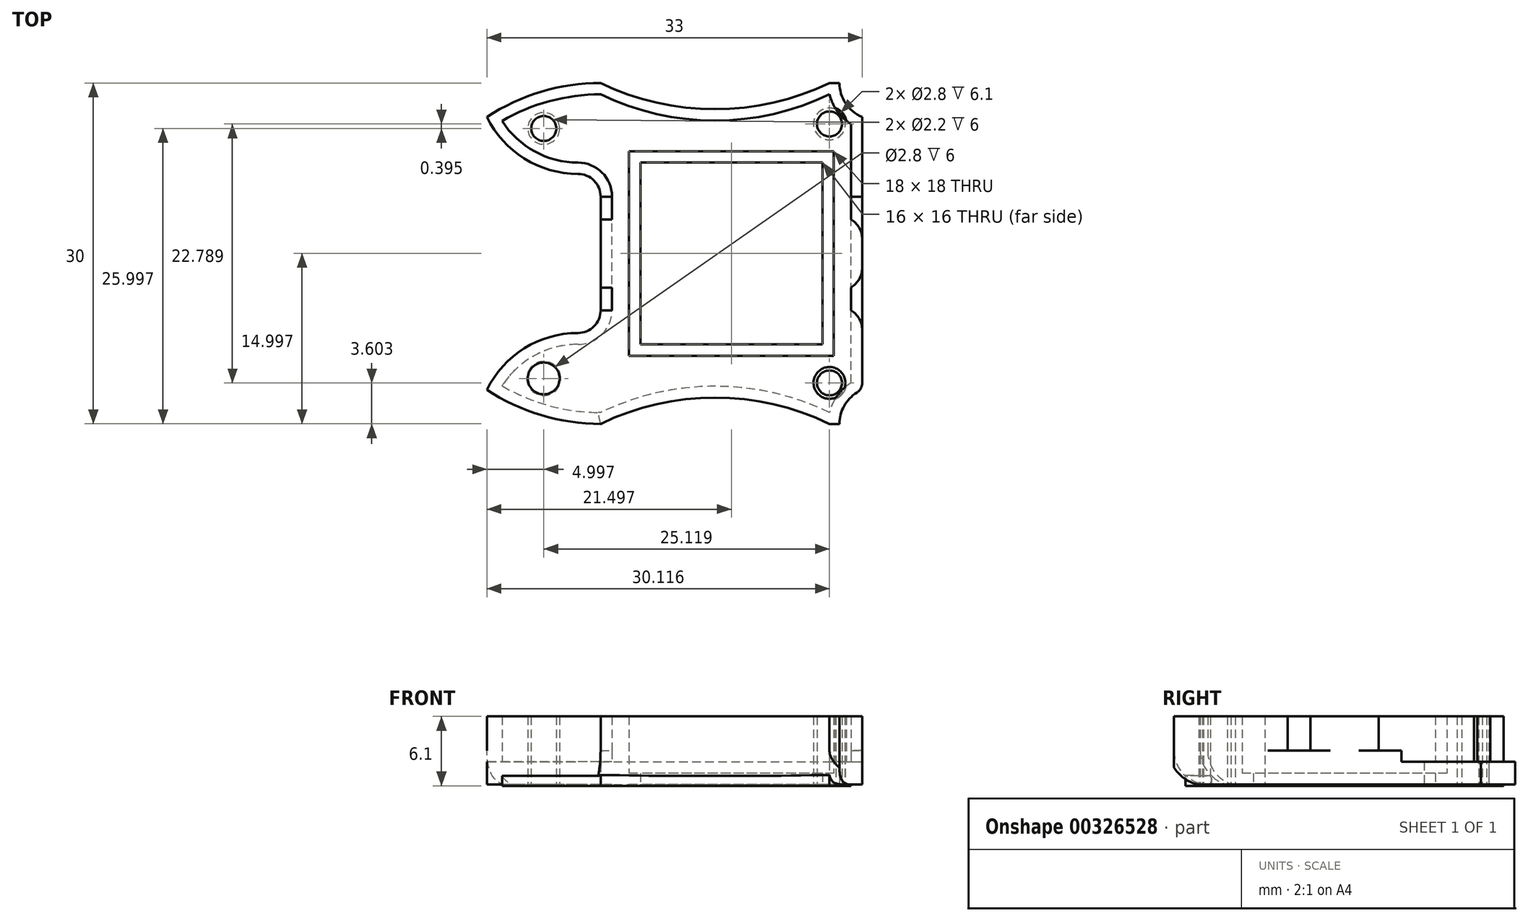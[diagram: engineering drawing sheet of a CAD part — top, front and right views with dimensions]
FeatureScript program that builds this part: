
annotation { "Feature Type Name" : "Feature", "Feature Type Description" : "" }
export const myFeature = defineFeature(function(context is Context, id is Id, definition is map)
    precondition{}
    {
        {
            var Q0;
            Q0=qCreatedBy(makeId("Top.planeOp"),FACE);
            var sketch = newSketch(context, id + "F0", { "sketchPlane" : qUnion([Q0])});
            skArc(sketch, "E0.MirrorCS", {"start": v(-70, 2.38) * mm, "mid": v(-65.22, 4.61) * mm, "end": v(-60, 5.38) * mm});
            skArc(sketch, "E1.MirrorCS", {"start": v(-62, -2.62) * mm, "mid": v(-66.72, -1.27) * mm, "end": v(-70, 2.38) * mm});
            skArc(sketch, "E2.MirrorCS", {"start": v(-62, -16.62) * mm, "mid": v(-66.72, -17.98) * mm, "end": v(-70, -21.62) * mm});
            skArc(sketch, "E3.MirrorCS", {"start": v(-70, -21.62) * mm, "mid": v(-65.22, -23.86) * mm, "end": v(-60, -24.62) * mm});
            skArc(sketch, "E4.MirrorCS", {"start": v(-62, -16.62) * mm, "mid": v(-60.59, -16.04) * mm, "end": v(-60, -14.62) * mm});
            skArc(sketch, "E5.MirrorCS", {"start": v(-62, -2.62) * mm, "mid": v(-60.59, -3.2) * mm, "end": v(-60, -4.62) * mm});
            skArc(sketch, "E6.MirrorCS", {"start": v(-37, -21.62) * mm, "mid": v(-38.46, -22.82) * mm, "end": v(-39, -24.62) * mm});
            skArc(sketch, "E7.MirrorCS", {"start": v(-37, 2.38) * mm, "mid": v(-38.46, 3.57) * mm, "end": v(-39, 5.38) * mm});
            skLineSegment(sketch, "E8", {"start": v(-37, 2.38) * mm, "end": v(-37, -4.62) * mm});
            skLineSegment(sketch, "E9", {"start": v(-37, -21.62) * mm, "end": v(-37, -14.62) * mm});
            skLineSegment(sketch, "E10", {"start": v(-39.88, -24.62) * mm, "end": v(-39, -24.62) * mm});
            skLineSegment(sketch, "E11", {"start": v(-39, 5.38) * mm, "end": v(-39.88, 5.38) * mm});
            skLineSegment(sketch, "E12", {"start": v(-37, -14.62) * mm, "end": v(-37, -4.62) * mm});
            skLineSegment(sketch, "E13", {"start": v(-60, -14.62) * mm, "end": v(-60, -4.62) * mm});
            skLineSegment(sketch, "E14.trimOffspring", {"start": v(-60, -4.62) * mm, "end": v(-59, -4.62) * mm});
            skLineSegment(sketch, "E15.trimOffspring", {"start": v(-60, -14.62) * mm, "end": v(-59, -14.62) * mm});
            skArc(sketch, "E16.0", {"start": v(-62, -1.62) * mm, "mid": v(-65.8, -0.65) * mm, "end": v(-68.67, 2.03) * mm});
            skArc(sketch, "E16.1", {"start": v(-62, -1.62) * mm, "mid": v(-59.88, -2.5) * mm, "end": v(-59, -4.62) * mm});
            skLineSegment(sketch, "E16.2", {"start": v(-59, -14.62) * mm, "end": v(-59, -4.62) * mm});
            skLineSegment(sketch, "E16.3", {"start": v(-38, -14.62) * mm, "end": v(-38, -4.62) * mm});
            skLineSegment(sketch, "E16.4", {"start": v(-38, 1.77) * mm, "end": v(-38, -4.62) * mm});
            skArc(sketch, "E16.5", {"start": v(-38, 1.77) * mm, "mid": v(-39.2, 2.89) * mm, "end": v(-39.88, 4.38) * mm});
            skLineSegment(sketch, "E16.7", {"start": v(-38, -21.02) * mm, "end": v(-38, -14.62) * mm});
            skArc(sketch, "E16.8", {"start": v(-38, -21.02) * mm, "mid": v(-39.2, -22.14) * mm, "end": v(-39.88, -23.62) * mm});
            skArc(sketch, "E16.10", {"start": v(-68.67, 2.03) * mm, "mid": v(-64.49, 3.78) * mm, "end": v(-60, 4.38) * mm});
            skArc(sketch, "E16.11", {"start": v(-68.67, -21.28) * mm, "mid": v(-64.49, -23.03) * mm, "end": v(-60, -23.62) * mm});
            skArc(sketch, "E16.12", {"start": v(-62, -17.62) * mm, "mid": v(-65.8, -18.6) * mm, "end": v(-68.67, -21.28) * mm});
            skArc(sketch, "E16.13", {"start": v(-62, -17.62) * mm, "mid": v(-59.88, -16.74) * mm, "end": v(-59, -14.62) * mm});
            skPoint(sketch, "E17", {"position": v(-65, 1.38) * mm});
            skPoint(sketch, "E18", {"position": v(-39.88, 1.77) * mm});
            skPoint(sketch, "E19.orphan", {"position": v(-70, 5.38) * mm});
            skLineSegment(sketch, "E20.trimOffspring", {"start": v(-60, -2.39) * mm, "end": v(-60, -2.62) * mm, "construction": true});
            skPoint(sketch, "E21.orphan", {"position": v(-60, 1.38) * mm});
            skPoint(sketch, "E22.start.orphan", {"position": v(-65, 5.38) * mm});
            skPoint(sketch, "E23.right.start.orphan", {"position": v(-70, 1.38) * mm});
            skPoint(sketch, "E23.top.end.orphan", {"position": v(-70, -2.62) * mm});
            skPoint(sketch, "E24.trimOffspring.end.orphan", {"position": v(-65, -2.62) * mm});
            skCircle(sketch, "E25", {"center": v(-65, 1.38) * mm, "radius": 1.5 * mm});
            skCircle(sketch, "E26", {"center": v(-39.88, 1.77) * mm, "radius": 1.5 * mm});
            skCircle(sketch, "E27.MirrorC", {"center": v(-65, -20.62) * mm, "radius": 1.5 * mm});
            skCircle(sketch, "E28.MirrorC", {"center": v(-39.88, -21.02) * mm, "radius": 1.5 * mm});
            skCircle(sketch, "E29.0", {"center": v(-65, -20.62) * mm, "radius": 1.4 * mm});
            skCircle(sketch, "E30.0", {"center": v(-39.88, -21.02) * mm, "radius": 1.4 * mm});
            skCircle(sketch, "E31.0", {"center": v(-39.88, 1.77) * mm, "radius": 1.4 * mm});
            skCircle(sketch, "E32.0", {"center": v(-65, 1.38) * mm, "radius": 1.4 * mm});
            skLineSegment(sketch, "E33", {"start": v(-60, -12.62) * mm, "end": v(-59, -12.62) * mm});
            skLineSegment(sketch, "E34", {"start": v(-60, -6.62) * mm, "end": v(-59, -6.62) * mm});
            skLineSegment(sketch, "E35.trimOffspring", {"start": v(-38, -12.62) * mm, "end": v(-37, -12.62) * mm});
            skLineSegment(sketch, "E36.trimOffspring", {"start": v(-38, -14.62) * mm, "end": v(-37, -14.62) * mm});
            skLineSegment(sketch, "E37.trimOffspring", {"start": v(-38, -6.62) * mm, "end": v(-37, -6.62) * mm});
            skPoint(sketch, "E38", {"position": v(-49.5, -22.31) * mm});
            skPoint(sketch, "E39", {"position": v(-49.5, -21.31) * mm});
            skArc(sketch, "E40", {"start": v(-39.88, -23.62) * mm, "mid": v(-49.94, -21.31) * mm, "end": v(-60, -23.62) * mm});
            skPoint(sketch, "E41", {"position": v(-39.88, -24.62) * mm});
            skArc(sketch, "E42", {"start": v(-39.88, -24.62) * mm, "mid": v(-49.94, -22.31) * mm, "end": v(-60, -24.62) * mm});
            skArc(sketch, "E43.MirrorCS", {"start": v(-39.88, 5.38) * mm, "mid": v(-49.94, 3.06) * mm, "end": v(-60, 5.38) * mm});
            skArc(sketch, "E44.MirrorCS", {"start": v(-39.88, 4.38) * mm, "mid": v(-49.94, 2.06) * mm, "end": v(-60, 4.38) * mm});
            skPoint(sketch, "E45", {"position": v(-48.5, -9.62) * mm});
            skLineSegment(sketch, "E46.bottom", {"start": v(-39.5, -0.62) * mm, "end": v(-57.5, -0.62) * mm});
            skLineSegment(sketch, "E46.top", {"start": v(-39.5, -18.62) * mm, "end": v(-57.5, -18.62) * mm});
            skLineSegment(sketch, "E46.left", {"start": v(-39.5, -0.62) * mm, "end": v(-39.5, -18.62) * mm});
            skLineSegment(sketch, "E46.right", {"start": v(-57.5, -0.62) * mm, "end": v(-57.5, -18.62) * mm});
            skLineSegment(sketch, "E47.trimOffspring", {"start": v(-38, -4.62) * mm, "end": v(-37, -4.62) * mm});
            skLineSegment(sketch, "E48.0", {"start": v(-40.5, -1.62) * mm, "end": v(-56.5, -1.62) * mm});
            skLineSegment(sketch, "E48.1", {"start": v(-40.5, -1.62) * mm, "end": v(-40.5, -17.62) * mm});
            skLineSegment(sketch, "E48.2", {"start": v(-40.5, -17.62) * mm, "end": v(-56.5, -17.62) * mm});
            skLineSegment(sketch, "E48.3", {"start": v(-56.5, -1.62) * mm, "end": v(-56.5, -17.62) * mm});
            skCircle(sketch, "E49.0", {"center": v(-65, -20.62) * mm, "radius": 1.1 * mm});
            skCircle(sketch, "E50.0", {"center": v(-39.88, 1.77) * mm, "radius": 1.1 * mm});
            skCircle(sketch, "E51.0", {"center": v(-65, 1.38) * mm, "radius": 1.1 * mm});
            skCircle(sketch, "E52.0", {"center": v(-39.88, -21.02) * mm, "radius": 1.1 * mm});
            skSolve(sketch);
        }
        {
            var Q0;
            Q0=makeQuery(id+"F0.imprint","IMPRINT",FACE,{"disambiguationData":[TD([[makeQuery(id+"F0.imprint","IMPRINT",EDGE,{"derivedFrom":sQuery(id+"F0.wireOp",EDGE,"E16.0")}),-1.0]])]});
            var Q1;
            {var subQ0=sQuery(id+"F0.wireOp",EDGE,"E16.2");Q1=makeQuery(id+"F0.imprint","IMPRINT",FACE,{"disambiguationData":[TD([[makeQuery(id+"F0.imprint","IMPRINT",EDGE,{"derivedFrom":subQ0}),-1.0]])]});}
            var Q2;
            {var subQ2=sQuery(id+"F0.wireOp",EDGE,"E16.7");Q2=makeQuery(id+"F0.imprint","IMPRINT",FACE,{"disambiguationData":[TD([[makeQuery(id+"F0.imprint","IMPRINT",EDGE,{"derivedFrom":subQ2}),1.0]])]});}
            var Q3;
            Q3=makeQuery(id+"F0.imprint","IMPRINT",FACE,{"disambiguationData":[TD([[makeQuery(id+"F0.imprint","IMPRINT",EDGE,{"derivedFrom":sQuery(id+"F0.wireOp",EDGE,"E27.MirrorC")}),-1.0]])]});
            var Q4;
            Q4=makeQuery(id+"F0.imprint","IMPRINT",FACE,{"disambiguationData":[TD([[makeQuery(id+"F0.imprint","IMPRINT",EDGE,{"derivedFrom":sQuery(id+"F0.wireOp",EDGE,"E25")}),1.0]])]});
            var Q5;
            {var subQ0=sQuery(id+"F0.wireOp",EDGE,"E26");var subQ1=sQuery(id+"F0.wireOp",EDGE,"E16.5");var subQ2=makeQuery(id+"F0.imprint","INTERSECT",VERTEX,{"disambiguationData":[OD(0.0)],"derivedFrom":[subQ1,subQ0]});Q5=makeQuery(id+"F0.imprint","IMPRINT",FACE,{"disambiguationData":[TD([[makeQuery(id+"F0.imprint","IMPRINT",EDGE,{"disambiguationData":[TD([[subQ2,-1.0]])],"derivedFrom":subQ1}),1.0]])]});}
            var Q6;
            {var subQ0=sQuery(id+"F0.wireOp",EDGE,"E28.MirrorC");var subQ1=sQuery(id+"F0.wireOp",EDGE,"E16.8");var subQ2=makeQuery(id+"F0.imprint","INTERSECT",VERTEX,{"disambiguationData":[OD(0.0)],"derivedFrom":[subQ1,subQ0]});Q6=makeQuery(id+"F0.imprint","IMPRINT",FACE,{"disambiguationData":[TD([[makeQuery(id+"F0.imprint","IMPRINT",EDGE,{"disambiguationData":[TD([[subQ2,-1.0]])],"derivedFrom":subQ1}),-1.0]])]});}
            var Q7;
            {var subQ0=sQuery(id+"F0.wireOp",EDGE,"E26");var subQ1=sQuery(id+"F0.wireOp",EDGE,"E16.5");var subQ2=makeQuery(id+"F0.imprint","INTERSECT",VERTEX,{"disambiguationData":[OD(0.0)],"derivedFrom":[subQ1,subQ0]});Q7=makeQuery(id+"F0.imprint","IMPRINT",FACE,{"disambiguationData":[TD([[makeQuery(id+"F0.imprint","IMPRINT",EDGE,{"disambiguationData":[TD([[subQ2,-1.0]])],"derivedFrom":subQ1}),-1.0]])]});}
            var Q8;
            {var subQ0=sQuery(id+"F0.wireOp",EDGE,"E28.MirrorC");var subQ1=sQuery(id+"F0.wireOp",EDGE,"E16.8");var subQ2=makeQuery(id+"F0.imprint","INTERSECT",VERTEX,{"disambiguationData":[OD(0.0)],"derivedFrom":[subQ1,subQ0]});Q8=makeQuery(id+"F0.imprint","IMPRINT",FACE,{"disambiguationData":[TD([[makeQuery(id+"F0.imprint","IMPRINT",EDGE,{"disambiguationData":[TD([[subQ2,-1.0]])],"derivedFrom":subQ1}),1.0]])]});}
            extrude(context, id + "F1", {"entities" : qUnion([Q0, Q1, Q2, Q3, Q4, Q5, Q6, Q7, Q8]), "depth" : 2 * mm});
        }
        {
            var Q0;
            Q0=makeQuery(id+"F0.imprint","IMPRINT",FACE,{"disambiguationData":[TD([[makeQuery(id+"F0.imprint","IMPRINT",EDGE,{"derivedFrom":sQuery(id+"F0.wireOp",EDGE,"E0.MirrorCS")}),-1.0]])]});
            var Q1;
            Q1=makeQuery(id+"F0.imprint","IMPRINT",FACE,{"disambiguationData":[TD([[makeQuery(id+"F0.imprint","IMPRINT",EDGE,{"derivedFrom":sQuery(id+"F0.wireOp",EDGE,"E2.MirrorCS")}),1.0]])]});
            var Q2;
            {var subQ0=sQuery(id+"F0.wireOp",EDGE,"E33");Q2=makeQuery(id+"F0.imprint","IMPRINT",FACE,{"disambiguationData":[TD([[makeQuery(id+"F0.imprint","IMPRINT",EDGE,{"derivedFrom":subQ0}),1.0]])]});}
            var Q3;
            {var subQ0=sQuery(id+"F0.wireOp",EDGE,"E35.trimOffspring");Q3=makeQuery(id+"F0.imprint","IMPRINT",FACE,{"disambiguationData":[TD([[makeQuery(id+"F0.imprint","IMPRINT",EDGE,{"derivedFrom":subQ0}),1.0]])]});}
            extrude(context, id + "F2", {"entities" : qUnion([Q0, Q1, Q2, Q3]), "operationType" : NewBodyOperationType.ADD, "depth" : 6 * mm});
        }
        {
            var Q0;
            {var subQ0=sQuery(id+"F0.wireOp",EDGE,"E13");Q0=makeQuery(id+"F0.imprint","IMPRINT",FACE,{"disambiguationData":[TD([[makeQuery(id+"F0.imprint","IMPRINT",EDGE,{"derivedFrom":subQ0}),-1.0]])]});}
            var Q1;
            {var subQ0=sQuery(id+"F0.wireOp",EDGE,"E12");Q1=makeQuery(id+"F0.imprint","IMPRINT",FACE,{"disambiguationData":[TD([[makeQuery(id+"F0.imprint","IMPRINT",EDGE,{"derivedFrom":subQ0}),1.0]])]});}
            extrude(context, id + "F3", {"entities" : qUnion([Q0, Q1]), "operationType" : NewBodyOperationType.ADD, "depth" : 3 * mm});
        }
        {
            var Q0;
            Q0=makeQuery(id+"F0.imprint","IMPRINT",FACE,{"disambiguationData":[TD([[makeQuery(id+"F0.imprint","IMPRINT",EDGE,{"derivedFrom":sQuery(id+"F0.wireOp",EDGE,"E25")}),1.0]])]});
            var Q1;
            Q1=makeQuery(id+"F0.imprint","IMPRINT",FACE,{"disambiguationData":[TD([[makeQuery(id+"F0.imprint","IMPRINT",EDGE,{"derivedFrom":sQuery(id+"F0.wireOp",EDGE,"E27.MirrorC")}),-1.0]])]});
            var Q2;
            {var subQ0=sQuery(id+"F0.wireOp",EDGE,"E28.MirrorC");var subQ1=sQuery(id+"F0.wireOp",EDGE,"E16.8");var subQ2=makeQuery(id+"F0.imprint","INTERSECT",VERTEX,{"disambiguationData":[OD(0.0)],"derivedFrom":[subQ1,subQ0]});Q2=makeQuery(id+"F0.imprint","IMPRINT",FACE,{"disambiguationData":[TD([[makeQuery(id+"F0.imprint","IMPRINT",EDGE,{"disambiguationData":[TD([[subQ2,-1.0]])],"derivedFrom":subQ1}),-1.0]])]});}
            var Q3;
            {var subQ0=sQuery(id+"F0.wireOp",EDGE,"E26");var subQ1=sQuery(id+"F0.wireOp",EDGE,"E16.5");var subQ2=makeQuery(id+"F0.imprint","INTERSECT",VERTEX,{"disambiguationData":[OD(0.0)],"derivedFrom":[subQ1,subQ0]});Q3=makeQuery(id+"F0.imprint","IMPRINT",FACE,{"disambiguationData":[TD([[makeQuery(id+"F0.imprint","IMPRINT",EDGE,{"disambiguationData":[TD([[subQ2,-1.0]])],"derivedFrom":subQ1}),1.0]])]});}
            var Q4;
            {var subQ0=sQuery(id+"F0.wireOp",EDGE,"E26");var subQ1=sQuery(id+"F0.wireOp",EDGE,"E16.5");var subQ2=makeQuery(id+"F0.imprint","INTERSECT",VERTEX,{"disambiguationData":[OD(0.0)],"derivedFrom":[subQ1,subQ0]});Q4=makeQuery(id+"F0.imprint","IMPRINT",FACE,{"disambiguationData":[TD([[makeQuery(id+"F0.imprint","IMPRINT",EDGE,{"disambiguationData":[TD([[subQ2,-1.0]])],"derivedFrom":subQ1}),-1.0]])]});}
            var Q5;
            {var subQ0=sQuery(id+"F0.wireOp",EDGE,"E28.MirrorC");var subQ1=sQuery(id+"F0.wireOp",EDGE,"E16.8");var subQ2=makeQuery(id+"F0.imprint","INTERSECT",VERTEX,{"disambiguationData":[OD(0.0)],"derivedFrom":[subQ1,subQ0]});Q5=makeQuery(id+"F0.imprint","IMPRINT",FACE,{"disambiguationData":[TD([[makeQuery(id+"F0.imprint","IMPRINT",EDGE,{"disambiguationData":[TD([[subQ2,-1.0]])],"derivedFrom":subQ1}),1.0]])]});}
            extrude(context, id + "F4", {"entities" : qUnion([Q0, Q1, Q2, Q3, Q4, Q5]), "operationType" : NewBodyOperationType.ADD, "oppositeDirection" : true, "depth" : 0.1 * mm});
        }
        {
            var Q0;
            Q0=makeQuery(id+"F4.opExtrude","CAP_FACE",FACE,{"disambiguationData":[OSD([sQuery(id+"F0.wireOp",EDGE,"E25"),sQuery(id+"F0.wireOp",EDGE,"E32.0")])],"isStart":false});
            var Q1;
            Q1=makeQuery(id+"F4.opExtrude","CAP_FACE",FACE,{"disambiguationData":[OSD([sQuery(id+"F0.wireOp",EDGE,"E26"),sQuery(id+"F0.wireOp",EDGE,"E31.0")])],"isStart":false});
            var Q2;
            Q2=makeQuery(id+"F4.opExtrude","CAP_FACE",FACE,{"disambiguationData":[OSD([sQuery(id+"F0.wireOp",EDGE,"E28.MirrorC"),sQuery(id+"F0.wireOp",EDGE,"E30.0")])],"isStart":false});
            var Q3;
            Q3=makeQuery(id+"F4.opExtrude","CAP_FACE",FACE,{"disambiguationData":[OSD([sQuery(id+"F0.wireOp",EDGE,"E27.MirrorC"),sQuery(id+"F0.wireOp",EDGE,"E29.0")])],"isStart":false});
            extrude(context, id + "F5", {"entities" : qUnion([Q0, Q1, Q2, Q3]), "operationType" : NewBodyOperationType.ADD, "oppositeDirection" : true, "depth" : 6.1 * mm});
        }
        {
            var Q0;
            Q0=makeQuery(id+"F0.imprint","IMPRINT",FACE,{"disambiguationData":[TD([[makeQuery(id+"F0.imprint","IMPRINT",EDGE,{"derivedFrom":sQuery(id+"F0.wireOp",EDGE,"E46.bottom")}),1.0]])]});
            extrude(context, id + "F6", {"entities" : qUnion([Q0]), "operationType" : NewBodyOperationType.ADD, "depth" : 1 * mm});
        }
        {
            var Q0;
            Q0=makeQuery(id+"F2.opExtrude","CAP_EDGE",EDGE,{"disambiguationData":[OSD([sQuery(id+"F0.wireOp",EDGE,"E3.MirrorCS")])],"isStart":true});
            var Q1;
            Q1=makeQuery(id+"F2.opExtrude","CAP_EDGE",EDGE,{"disambiguationData":[OSD([sQuery(id+"F0.wireOp",EDGE,"E42")])],"isStart":true});
            var Q2;
            Q2=makeQuery(id+"F2.opExtrude","CAP_EDGE",EDGE,{"disambiguationData":[OSD([sQuery(id+"F0.wireOp",EDGE,"E0.MirrorCS")])],"isStart":true});
            var Q3;
            Q3=makeQuery(id+"F2.opExtrude","CAP_EDGE",EDGE,{"disambiguationData":[OSD([sQuery(id+"F0.wireOp",EDGE,"E43.MirrorCS")])],"isStart":true});
            fillet(context, id + "F7", {"entities" : qUnion([Q0, Q1, Q2, Q3]), "radius" : 3 * mm, "tangentPropagation" : true, "allowEdgeOverflow" : false});
        }
        {
            var Q0;
            Q0=makeQuery(id+"F2.opExtrude","SWEPT_EDGE",EDGE,{"disambiguationData":[OSD([sQuery(id+"F0.wireOp",EDGE,"E7.MirrorCS"),sQuery(id+"F0.wireOp",EDGE,"E8")])]});
            var Q1;
            Q1=makeQuery(id+"F2.opExtrude","SWEPT_EDGE",EDGE,{"disambiguationData":[OSD([sQuery(id+"F0.wireOp",EDGE,"E6.MirrorCS"),sQuery(id+"F0.wireOp",EDGE,"E9")])]});
            fillet(context, id + "F8", {"entities" : qUnion([Q0, Q1]), "radius" : 1 * mm, "tangentPropagation" : true, "allowEdgeOverflow" : false});
        }
        {
            var Q0;
            Q0=makeQuery(id+"F0.imprint","IMPRINT",FACE,{"disambiguationData":[TD([[makeQuery(id+"F0.imprint","IMPRINT",EDGE,{"derivedFrom":sQuery(id+"F0.wireOp",EDGE,"E32.0")}),1.0]])]});
            var Q1;
            Q1=makeQuery(id+"F0.imprint","IMPRINT",FACE,{"disambiguationData":[TD([[makeQuery(id+"F0.imprint","IMPRINT",EDGE,{"derivedFrom":sQuery(id+"F0.wireOp",EDGE,"E50.0")}),-1.0]])]});
            var Q2;
            {var subQ0=sQuery(id+"F0.wireOp",EDGE,"E31.0");var subQ1=sQuery(id+"F0.wireOp",EDGE,"E16.5");var subQ2=makeQuery(id+"F0.imprint","INTERSECT",VERTEX,{"disambiguationData":[OD(0.0)],"derivedFrom":[subQ1,subQ0]});Q2=makeQuery(id+"F0.imprint","IMPRINT",FACE,{"disambiguationData":[TD([[makeQuery(id+"F0.imprint","IMPRINT",EDGE,{"disambiguationData":[TD([[subQ2,-1.0]])],"derivedFrom":subQ1}),-1.0]])]});}
            var Q3;
            Q3=makeQuery(id+"F0.imprint","IMPRINT",FACE,{"disambiguationData":[TD([[makeQuery(id+"F0.imprint","IMPRINT",EDGE,{"derivedFrom":sQuery(id+"F0.wireOp",EDGE,"E52.0")}),1.0]])]});
            var Q4;
            {var subQ0=sQuery(id+"F0.wireOp",EDGE,"E30.0");var subQ1=sQuery(id+"F0.wireOp",EDGE,"E16.8");var subQ2=makeQuery(id+"F0.imprint","INTERSECT",VERTEX,{"disambiguationData":[OD(0.0)],"derivedFrom":[subQ1,subQ0]});Q4=makeQuery(id+"F0.imprint","IMPRINT",FACE,{"disambiguationData":[TD([[makeQuery(id+"F0.imprint","IMPRINT",EDGE,{"disambiguationData":[TD([[subQ2,-1.0]])],"derivedFrom":subQ1}),1.0]])]});}
            var Q5;
            Q5=makeQuery(id+"F0.imprint","IMPRINT",FACE,{"disambiguationData":[TD([[makeQuery(id+"F0.imprint","IMPRINT",EDGE,{"derivedFrom":sQuery(id+"F0.wireOp",EDGE,"E29.0")}),-1.0]])]});
            extrude(context, id + "F9", {"entities" : qUnion([Q0, Q1, Q2, Q3, Q4, Q5]), "operationType" : NewBodyOperationType.ADD, "depth" : 6 * mm});
        }
        {
            var Q0;
            Q0=makeQuery(id+"F2.opExtrude","SWEPT_EDGE",EDGE,{"disambiguationData":[OSD([sQuery(id+"F0.wireOp",EDGE,"E8"),sQuery(id+"F0.wireOp",EDGE,"E12"),sQuery(id+"F0.wireOp",EDGE,"E47.trimOffspring")])]});
            var Q1;
            Q1=makeQuery(id+"F2.opExtrude","SWEPT_EDGE",EDGE,{"disambiguationData":[OSD([sQuery(id+"F0.wireOp",EDGE,"E9"),sQuery(id+"F0.wireOp",EDGE,"E12"),sQuery(id+"F0.wireOp",EDGE,"E36.trimOffspring")])]});
            fillet(context, id + "F10", {"entities" : qUnion([Q0, Q1]), "radius" : 2 * mm, "tangentPropagation" : true, "allowEdgeOverflow" : false});
        }
    });
